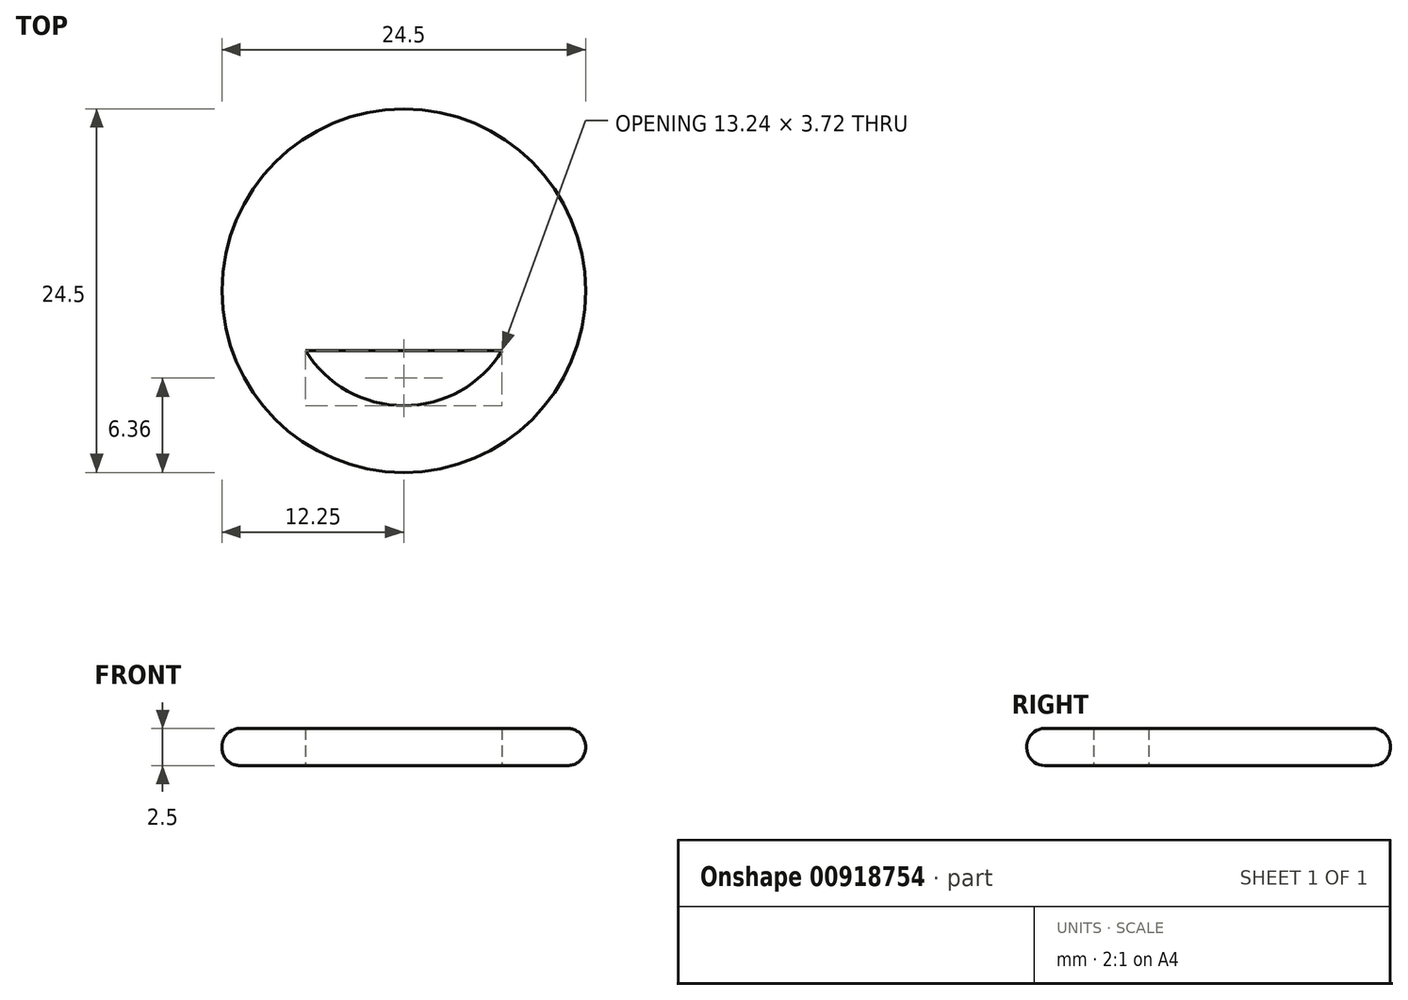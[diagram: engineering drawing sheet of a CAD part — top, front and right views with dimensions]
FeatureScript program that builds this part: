
annotation { "Feature Type Name" : "Feature", "Feature Type Description" : "" }
export const myFeature = defineFeature(function(context is Context, id is Id, definition is map)
    precondition{}
    {
        {
            var Q0;
            Q0=qCreatedBy(makeId("Top.planeOp"),FACE);
            var sketch = newSketch(context, id + "F0", { "sketchPlane" : qUnion([Q0])});
            skCircle(sketch, "E0", {"center": v(0, 0) * mm, "radius": 12.25 * mm});
            skArc(sketch, "E1.0", {"start": v(-6.62, -4.03) * mm, "mid": v(0, -7.75) * mm, "end": v(6.62, -4.03) * mm});
            skLineSegment(sketch, "E2", {"start": v(-6.62, -4.03) * mm, "end": v(6.62, -4.03) * mm});
            skSolve(sketch);
        }
        {
            var Q0;
            Q0=makeQuery(id+"F0.imprint","IMPRINT",FACE,{"disambiguationData":[TD([[makeQuery(id+"F0.imprint","IMPRINT",EDGE,{"derivedFrom":sQuery(id+"F0.wireOp",EDGE,"E0")}),1.0]])]});
            extrude(context, id + "F1", {"entities" : qUnion([Q0]), "depth" : 2.5 * mm, "offsetDistance" : 25 * mm});
        }
        {
            var Q0;
            Q0=makeQuery(id+"F1.opExtrude","CAP_EDGE",EDGE,{"disambiguationData":[OSD([sQuery(id+"F0.wireOp",EDGE,"E0")])],"isStart":false});
            var Q1;
            Q1=makeQuery(id+"F1.opExtrude","CAP_EDGE",EDGE,{"disambiguationData":[OSD([sQuery(id+"F0.wireOp",EDGE,"E0")])],"isStart":true});
            fillet(context, id + "F2", {"entities" : qUnion([Q0, Q1]), "radius" : 1.2 * mm, "tangentPropagation" : true, "allowEdgeOverflow" : false});
        }
    });
